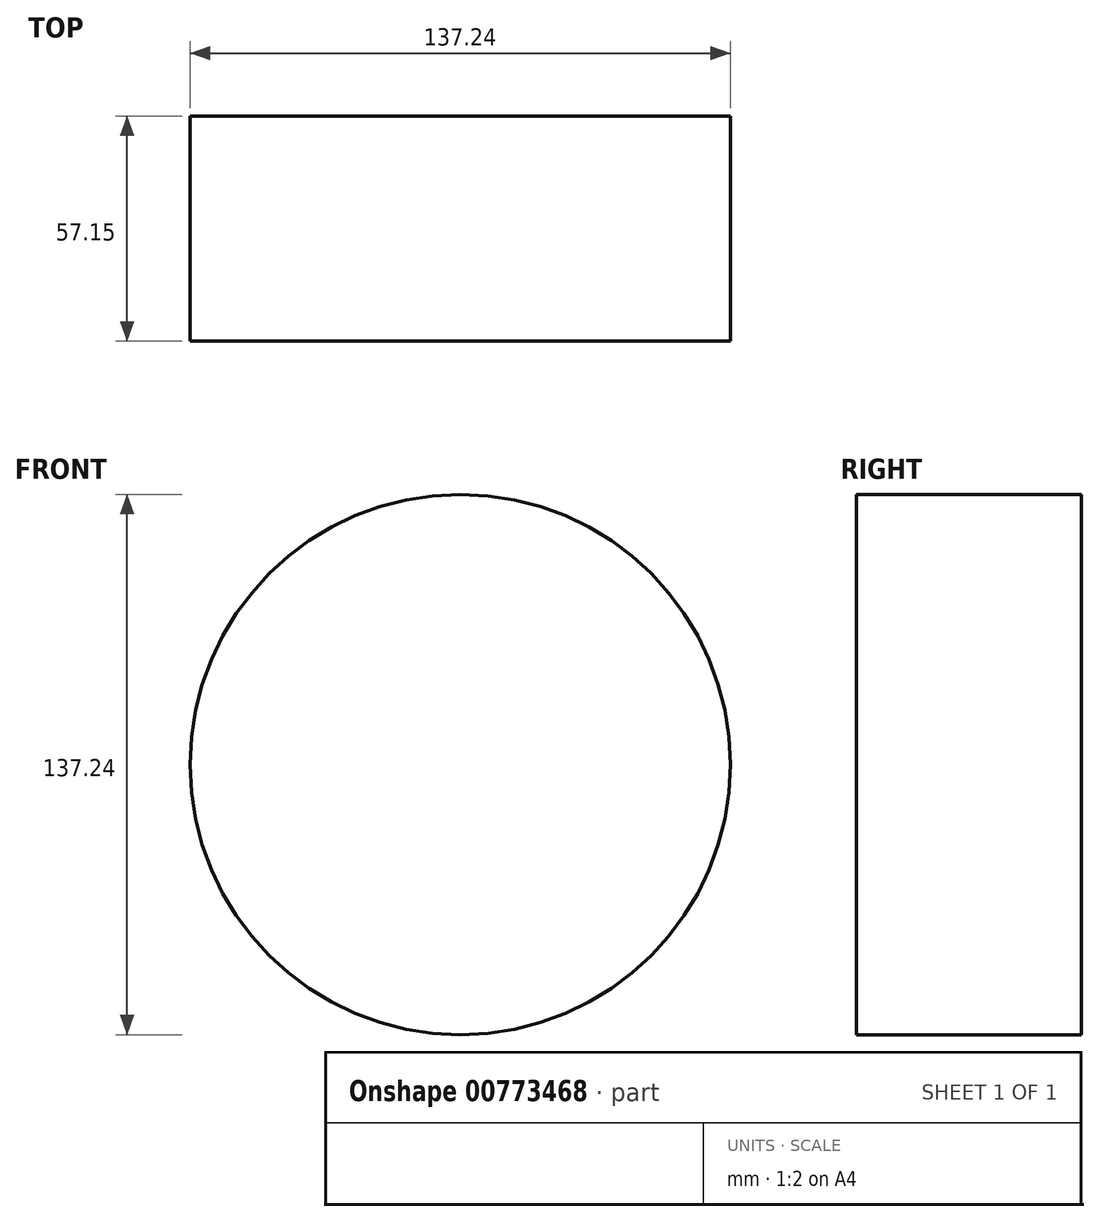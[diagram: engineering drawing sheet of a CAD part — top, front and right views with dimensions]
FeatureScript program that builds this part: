
annotation { "Feature Type Name" : "Feature", "Feature Type Description" : "" }
export const myFeature = defineFeature(function(context is Context, id is Id, definition is map)
    precondition{}
    {
        {
            var Q0;
            Q0=qCreatedBy(makeId("Front.planeOp"),FACE);
            var sketch = newSketch(context, id + "F0", { "sketchPlane" : qUnion([Q0])});
            skCircle(sketch, "E0", {"center": v(-6.95, 0) * mm, "radius": 68.62 * mm});
            skSolve(sketch);
        }
        {
            var Q0;
            Q0 = qSketchRegion(id + "F0", true);
            extrude(context, id + "F1", {"entities" : qUnion([Q0]), "depth" : 57.15 * mm, "offsetDistance" : 25.4 * mm});
        }
    });
